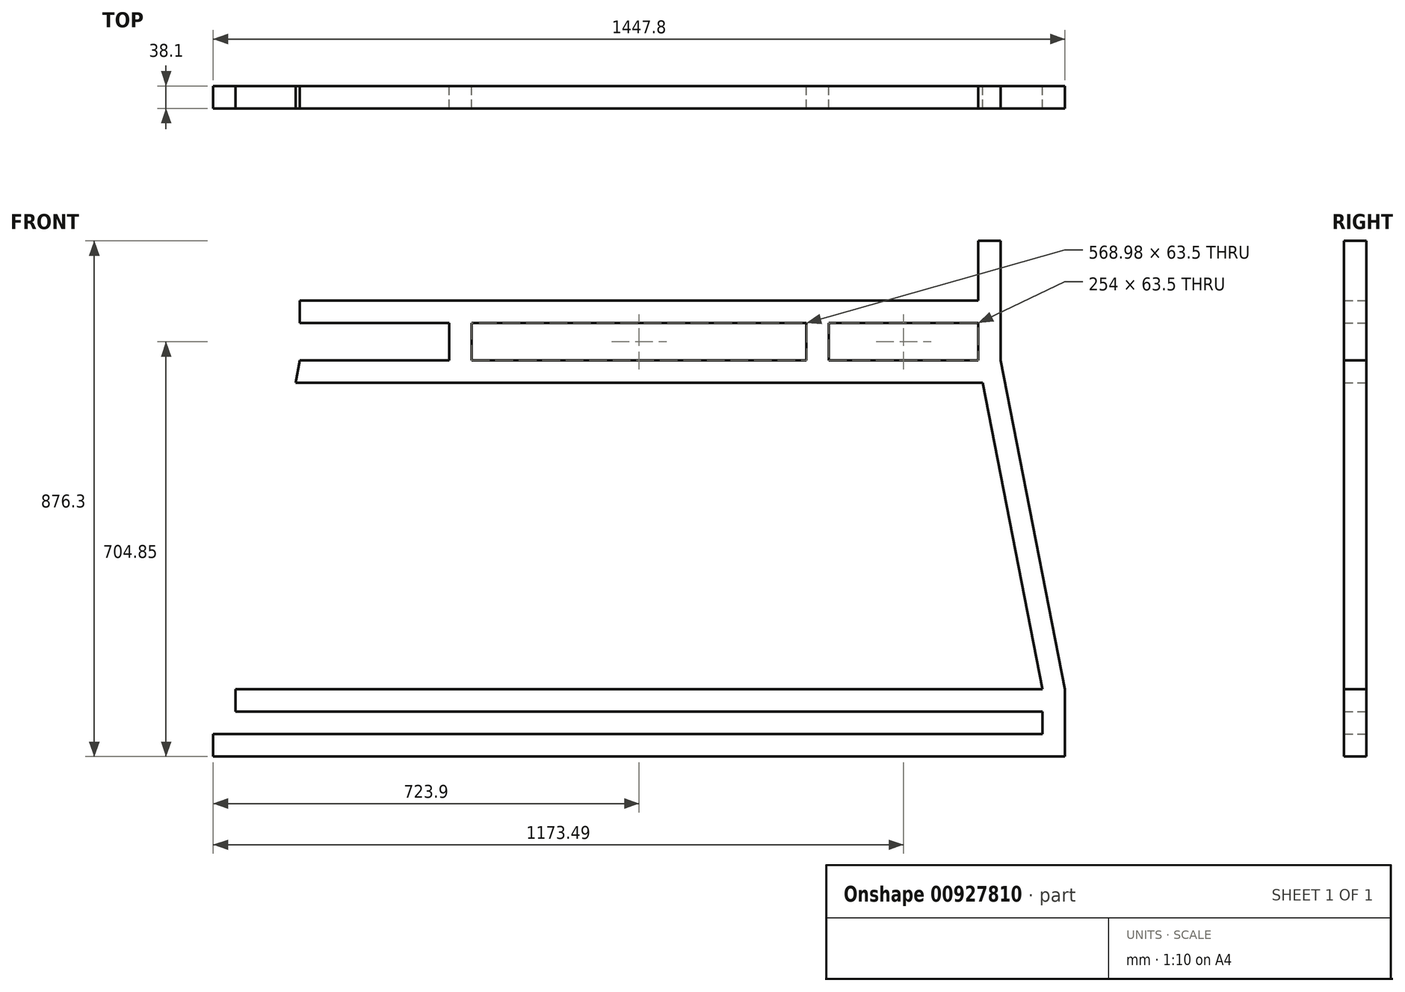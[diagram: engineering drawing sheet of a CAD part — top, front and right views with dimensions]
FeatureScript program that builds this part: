
annotation { "Feature Type Name" : "Feature", "Feature Type Description" : "" }
export const myFeature = defineFeature(function(context is Context, id is Id, definition is map)
    precondition{}
    {
        {
            var Q0;
            Q0=qCreatedBy(makeId("Front.planeOp"),FACE);
            var sketch = newSketch(context, id + "F0", { "sketchPlane" : qUnion([Q0])});
            skLineSegment(sketch, "E0", {"start": v(-742.62, 0) * mm, "end": v(723.9, 0) * mm});
            skLineSegment(sketch, "E1", {"start": v(723.9, 0) * mm, "end": v(723.9, 76.2) * mm});
            skLineSegment(sketch, "E2", {"start": v(723.9, 76.2) * mm, "end": v(614.7, 635) * mm});
            skLineSegment(sketch, "E3", {"start": v(614.7, 635) * mm, "end": v(614.7, 838.2) * mm});
            skLineSegment(sketch, "E4", {"start": v(614.7, 838.2) * mm, "end": v(576.6, 838.2) * mm});
            skLineSegment(sketch, "E5", {"start": v(576.6, 838.2) * mm, "end": v(576.6, 635) * mm});
            skLineSegment(sketch, "E6", {"start": v(576.6, 635) * mm, "end": v(685.8, 76.2) * mm});
            skLineSegment(sketch, "E7", {"start": v(685.8, 76.2) * mm, "end": v(685.8, 0) * mm});
            skLineSegment(sketch, "E8.MirrorCS", {"start": v(742.62, 0) * mm, "end": v(-723.9, 0) * mm});
            skLineSegment(sketch, "E9.MirrorCS", {"start": v(-576.6, 635) * mm, "end": v(-685.8, 76.2) * mm});
            skLineSegment(sketch, "E10.MirrorCS", {"start": v(-723.9, 0) * mm, "end": v(-723.9, 76.2) * mm});
            skLineSegment(sketch, "E11.MirrorCS", {"start": v(-576.6, 838.2) * mm, "end": v(-576.6, 635) * mm});
            skLineSegment(sketch, "E12.MirrorCS", {"start": v(-614.7, 838.2) * mm, "end": v(-576.6, 838.2) * mm});
            skLineSegment(sketch, "E13.MirrorCS", {"start": v(-614.7, 635) * mm, "end": v(-614.7, 838.2) * mm});
            skLineSegment(sketch, "E14.MirrorCS", {"start": v(-685.8, 76.2) * mm, "end": v(-685.8, 0) * mm});
            skLineSegment(sketch, "E15.MirrorCS", {"start": v(-723.9, 76.2) * mm, "end": v(-614.7, 635) * mm});
            skLineSegment(sketch, "E16", {"start": v(-576.6, 635) * mm, "end": v(576.6, 635) * mm});
            skLineSegment(sketch, "E17", {"start": v(-584.04, 596.9) * mm, "end": v(584.04, 596.9) * mm});
            skLineSegment(sketch, "E18", {"start": v(-685.8, 76.2) * mm, "end": v(685.8, 76.2) * mm});
            skLineSegment(sketch, "E19", {"start": v(-685.8, 38.1) * mm, "end": v(685.8, 38.1) * mm});
            skLineSegment(sketch, "E20", {"start": v(-723.9, 0) * mm, "end": v(-723.9, -38.1) * mm});
            skLineSegment(sketch, "E21", {"start": v(-723.9, -38.1) * mm, "end": v(723.9, -38.1) * mm});
            skLineSegment(sketch, "E22", {"start": v(723.9, -38.1) * mm, "end": v(723.9, 0) * mm});
            skLineSegment(sketch, "E23", {"start": v(-576.6, 698.5) * mm, "end": v(576.6, 698.5) * mm});
            skPoint(sketch, "E23.endSnap0", {"position": v(576.6, 736.6) * mm});
            skLineSegment(sketch, "E24", {"start": v(576.6, 698.5) * mm, "end": v(576.6, 736.6) * mm});
            skLineSegment(sketch, "E25", {"start": v(-576.6, 736.6) * mm, "end": v(576.6, 736.6) * mm});
            skLineSegment(sketch, "E26", {"start": v(-322.6, 698.5) * mm, "end": v(-322.6, 635) * mm});
            skLineSegment(sketch, "E27", {"start": v(-284.5, 698.5) * mm, "end": v(-284.5, 635) * mm});
            skLineSegment(sketch, "E28", {"start": v(284.5, 698.5) * mm, "end": v(284.5, 635) * mm});
            skLineSegment(sketch, "E29", {"start": v(322.6, 698.5) * mm, "end": v(322.6, 635) * mm});
            skLineSegment(sketch, "E30.MirrorCS", {"start": v(284.5, -774.7) * mm, "end": v(284.5, -711.2) * mm});
            skLineSegment(sketch, "E31.MirrorCS", {"start": v(-284.5, -774.7) * mm, "end": v(-284.5, -711.2) * mm});
            skLineSegment(sketch, "E32.MirrorCS", {"start": v(322.6, -774.7) * mm, "end": v(322.6, -711.2) * mm});
            skLineSegment(sketch, "E33.MirrorCS", {"start": v(-322.6, -774.7) * mm, "end": v(-322.6, -711.2) * mm});
            skSolve(sketch);
        }
        {
            var Q0;
            {var subQ11=sQuery(id+"F0.wireOp",EDGE,"E10.MirrorCS");Q0=makeQuery(id+"F0.imprint","IMPRINT",FACE,{"disambiguationData":[TD([[makeQuery(id+"F0.imprint","IMPRINT",EDGE,{"derivedFrom":subQ11}),-1.0]])]});}
            var Q1;
            {var subQ3=sQuery(id+"F0.wireOp",EDGE,"E17");Q1=makeQuery(id+"F0.imprint","IMPRINT",FACE,{"disambiguationData":[TD([[makeQuery(id+"F0.imprint","IMPRINT",EDGE,{"derivedFrom":subQ3}),1.0]])]});}
            var Q2;
            {var subQ8=sQuery(id+"F0.wireOp",EDGE,"E25");Q2=makeQuery(id+"F0.imprint","IMPRINT",FACE,{"disambiguationData":[TD([[makeQuery(id+"F0.imprint","IMPRINT",EDGE,{"derivedFrom":subQ8}),-1.0]])]});}
            var Q3;
            {var subQ9=sQuery(id+"F0.wireOp",EDGE,"E1");Q3=makeQuery(id+"F0.imprint","IMPRINT",FACE,{"disambiguationData":[TD([[makeQuery(id+"F0.imprint","IMPRINT",EDGE,{"derivedFrom":subQ9}),1.0]])]});}
            var Q4;
            {var subQ0=sQuery(id+"F0.wireOp",EDGE,"E18");Q4=makeQuery(id+"F0.imprint","IMPRINT",FACE,{"disambiguationData":[TD([[makeQuery(id+"F0.imprint","IMPRINT",EDGE,{"derivedFrom":subQ0}),-1.0]])]});}
            var Q5;
            {var subQ0=sQuery(id+"F0.wireOp",EDGE,"E20");Q5=makeQuery(id+"F0.imprint","IMPRINT",FACE,{"disambiguationData":[TD([[makeQuery(id+"F0.imprint","IMPRINT",EDGE,{"derivedFrom":subQ0}),1.0]])]});}
            extrude(context, id + "F1", {"entities" : qUnion([Q0, Q1, Q2, Q3, Q4, Q5]), "depth" : 38.1 * mm, "offsetDistance" : 25.4 * mm});
        }
        {
            var Q0;
            {var subQ8=sQuery(id+"F0.wireOp",EDGE,"E25");var subQ14=sQuery(id+"F0.wireOp",EDGE,"E20");var subQ21=sQuery(id+"F0.wireOp",EDGE,"E1");var subQ23=sQuery(id+"F0.wireOp",EDGE,"E10.MirrorCS");Q0=qUnion([makeQuery(id+"F0.imprint","IMPRINT",FACE,{"disambiguationData":[TD([[makeQuery(id+"F0.imprint","IMPRINT",EDGE,{"derivedFrom":subQ23}),-1.0]])]}),makeQuery(id+"F0.imprint","IMPRINT",FACE,{"disambiguationData":[TD([[makeQuery(id+"F0.imprint","IMPRINT",EDGE,{"derivedFrom":subQ21}),1.0]])]}),makeQuery(id+"F0.imprint","IMPRINT",FACE,{"disambiguationData":[TD([[makeQuery(id+"F0.imprint","IMPRINT",EDGE,{"derivedFrom":subQ14}),1.0]])]}),makeQuery(id+"F0.imprint","IMPRINT",FACE,{"disambiguationData":[TD([[makeQuery(id+"F0.imprint","IMPRINT",EDGE,{"derivedFrom":subQ8}),-1.0]])]})]);}
            var Q1;
            {var subQ2=sQuery(id+"F0.wireOp",EDGE,"E26");Q1=makeQuery(id+"F0.imprint","IMPRINT",FACE,{"disambiguationData":[TD([[makeQuery(id+"F0.imprint","IMPRINT",EDGE,{"derivedFrom":subQ2}),1.0]])]});}
            var Q2;
            {var subQ2=sQuery(id+"F0.wireOp",EDGE,"E28");Q2=makeQuery(id+"F0.imprint","IMPRINT",FACE,{"disambiguationData":[TD([[makeQuery(id+"F0.imprint","IMPRINT",EDGE,{"derivedFrom":subQ2}),1.0]])]});}
            extrude(context, id + "F2", {"entities" : qUnion([Q0, Q1, Q2]), "operationType" : NewBodyOperationType.ADD, "depth" : 38.1 * mm, "offsetDistance" : 25.4 * mm});
        }
    });
